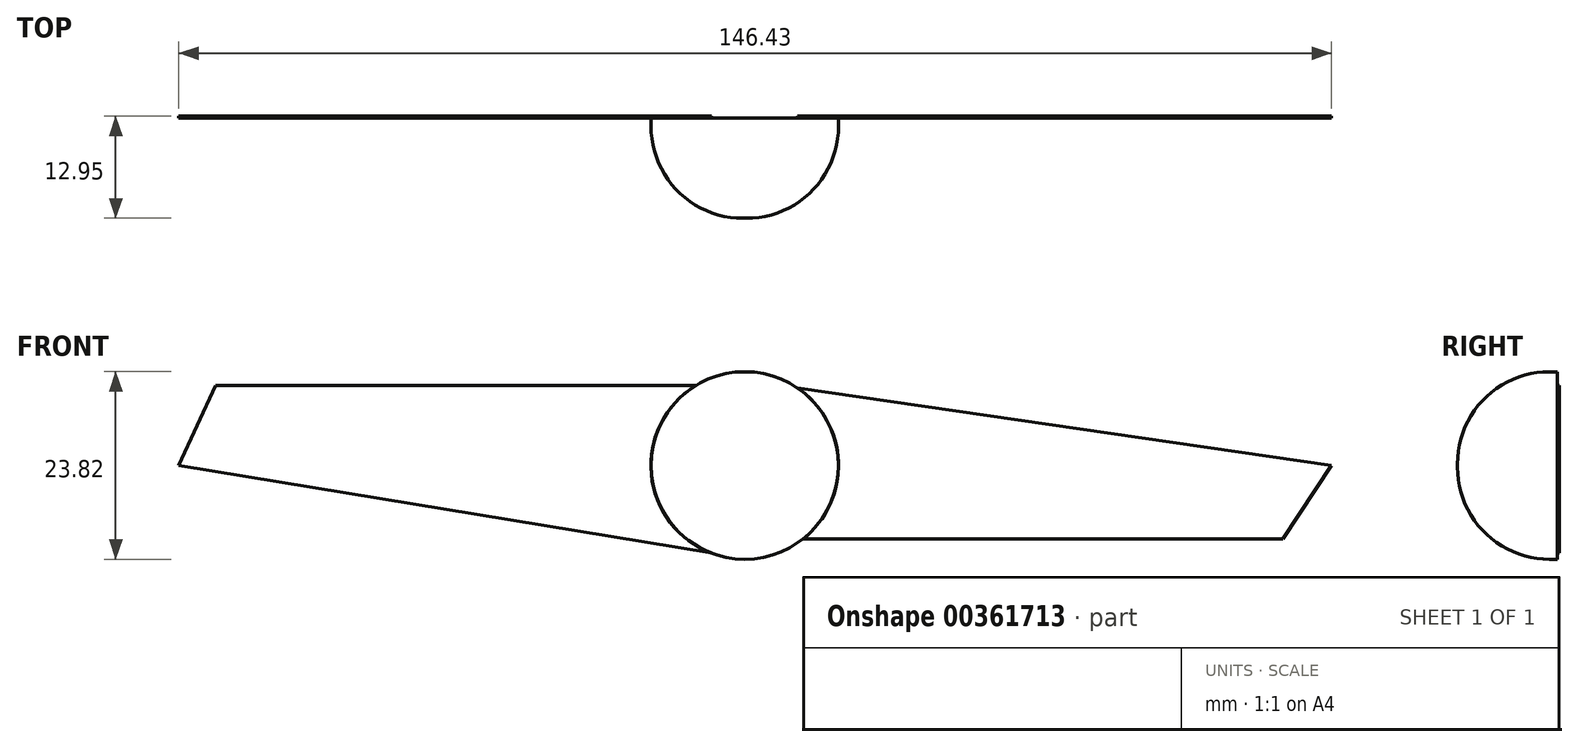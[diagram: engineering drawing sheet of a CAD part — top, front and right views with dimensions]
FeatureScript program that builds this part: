
annotation { "Feature Type Name" : "Feature", "Feature Type Description" : "" }
export const myFeature = defineFeature(function(context is Context, id is Id, definition is map)
    precondition{}
    {
        {
            var Q0;
            Q0=qCreatedBy(makeId("Front.planeOp"),FACE);
            var sketch = newSketch(context, id + "F0", { "sketchPlane" : qUnion([Q0])});
            skCircle(sketch, "E0", {"center": v(0, 0) * mm, "radius": 11.9 * mm});
            skLineSegment(sketch, "E1", {"start": v(7.41, -9.32) * mm, "end": v(68.37, -9.32) * mm});
            skLineSegment(sketch, "E2", {"start": v(-6.24, 10.14) * mm, "end": v(-67.2, 10.14) * mm});
            skLineSegment(sketch, "E3", {"start": v(68.37, -9.32) * mm, "end": v(74.54, 0) * mm});
            skLineSegment(sketch, "E4", {"start": v(0.88, 0) * mm, "end": v(0, 0) * mm});
            skLineSegment(sketch, "E5", {"start": v(-67.2, 10.14) * mm, "end": v(-71.9, 0) * mm});
            skLineSegment(sketch, "E6", {"start": v(74.54, 0) * mm, "end": v(6.67, 9.86) * mm});
            skLineSegment(sketch, "E7", {"start": v(-4.22, -11.13) * mm, "end": v(-71.9, 0) * mm});
            skSolve(sketch);
        }
        {
            var Q0;
            {var subQ0=sQuery(id+"F0.wireOp",EDGE,"E0");var subQ1=makeQuery(id+"F0.imprint","INTERSECT",VERTEX,{"derivedFrom":[subQ0,sQuery(id+"F0.wireOp",EDGE,"E2")]});Q0=makeQuery(id+"F0.imprint","IMPRINT",FACE,{"disambiguationData":[TD([[makeQuery(id+"F0.imprint","IMPRINT",EDGE,{"disambiguationData":[TD([[subQ1,1.0]])],"derivedFrom":subQ0}),1.0]])]});}
            extrude(context, id + "F1", {"entities" : qUnion([Q0]), "depth" : 12.7 * mm});
        }
        {
            var Q0;
            Q0=makeQuery(id+"F1.opExtrude","CAP_FACE",FACE,{"disambiguationData":[OSD([sQuery(id+"F0.wireOp",EDGE,"E0")])],"isStart":false});
            fillet(context, id + "F2", {"entities" : qUnion([Q0]), "radius" : 11.68 * mm, "tangentPropagation" : true, "allowEdgeOverflow" : false});
        }
        {
            var Q0;
            {var subQ0=sQuery(id+"F0.wireOp",EDGE,"E2");Q0=makeQuery(id+"F0.imprint","IMPRINT",FACE,{"disambiguationData":[TD([[makeQuery(id+"F0.imprint","IMPRINT",EDGE,{"derivedFrom":subQ0}),1.0]])]});}
            var Q1;
            {var subQ0=sQuery(id+"F0.wireOp",EDGE,"E1");Q1=makeQuery(id+"F0.imprint","IMPRINT",FACE,{"disambiguationData":[TD([[makeQuery(id+"F0.imprint","IMPRINT",EDGE,{"derivedFrom":subQ0}),1.0]])]});}
            extrude(context, id + "F3", {"entities" : qUnion([Q0, Q1]), "oppositeDirection" : true, "depth" : 0.25 * mm});
        }
    });
